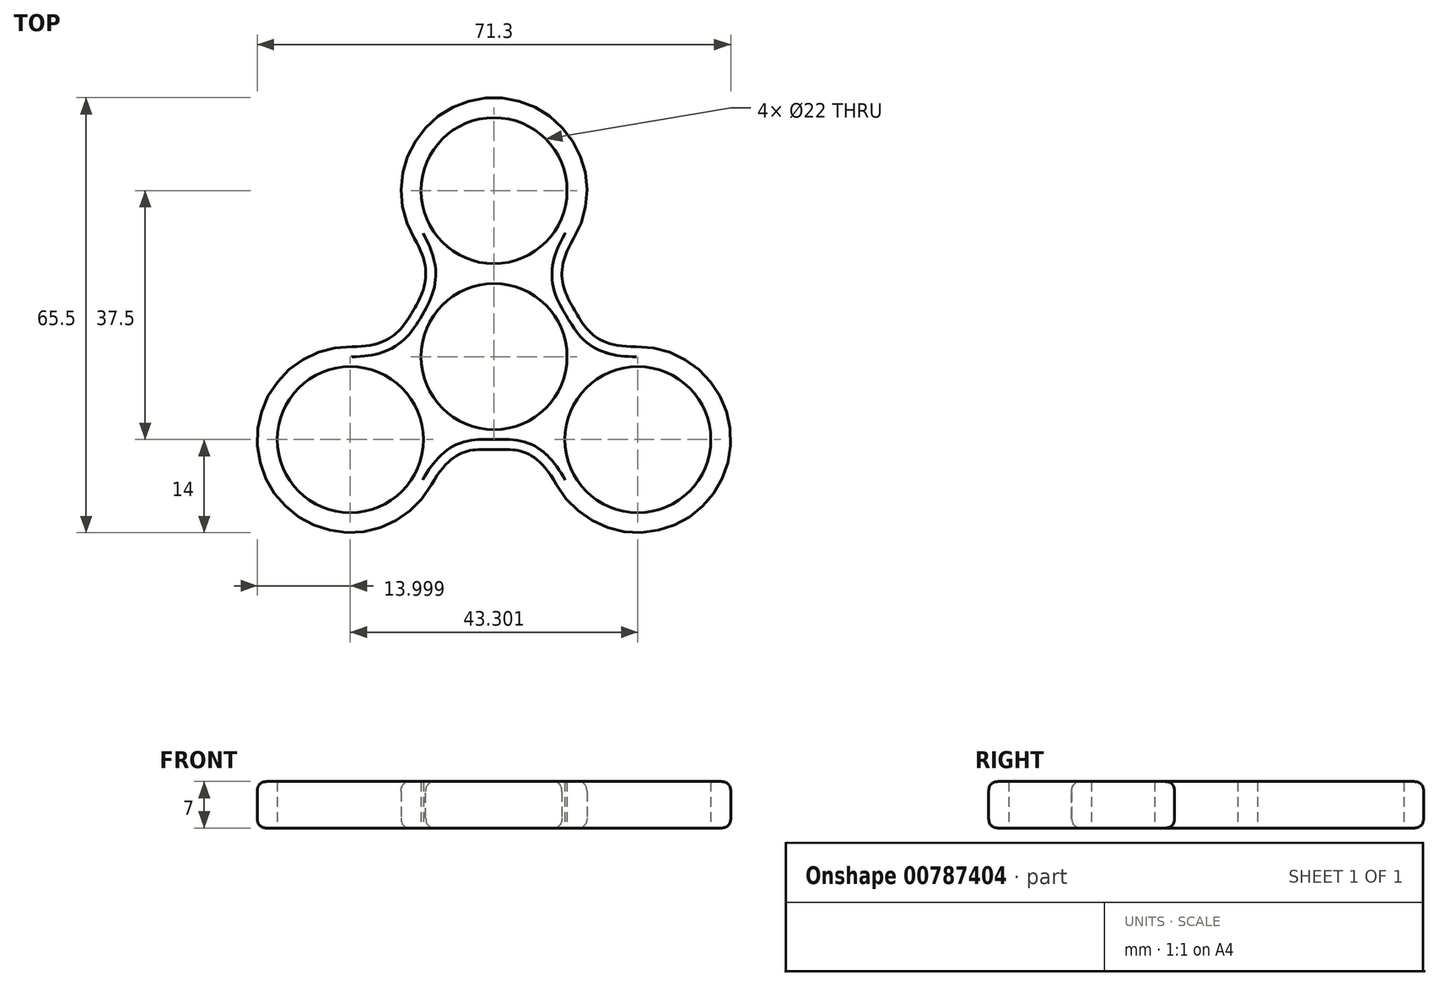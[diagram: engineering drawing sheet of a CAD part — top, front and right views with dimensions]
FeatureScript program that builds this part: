
annotation { "Feature Type Name" : "Feature", "Feature Type Description" : "" }
export const myFeature = defineFeature(function(context is Context, id is Id, definition is map)
    precondition{}
    {
        {
            var Q0;
            Q0=qCreatedBy(makeId("Top.planeOp"),FACE);
            var sketch = newSketch(context, id + "F0", { "sketchPlane" : qUnion([Q0])});
            skCircle(sketch, "E0", {"center": v(0, 0) * mm, "radius": 11 * mm});
            skLineSegment(sketch, "E1", {"start": v(0, 0) * mm, "end": v(0, 25) * mm});
            skLineSegment(sketch, "E2", {"start": v(0, 0) * mm, "end": v(-21.65, -12.5) * mm});
            skLineSegment(sketch, "E3", {"start": v(0, 0) * mm, "end": v(21.65, -12.5) * mm});
            skCircle(sketch, "E4", {"center": v(0, 25) * mm, "radius": 11 * mm});
            skCircle(sketch, "E5", {"center": v(-21.65, -12.5) * mm, "radius": 11 * mm});
            skCircle(sketch, "E6", {"center": v(21.65, -12.5) * mm, "radius": 11 * mm});
            skCircle(sketch, "E7", {"center": v(0, 25) * mm, "radius": 14 * mm});
            skCircle(sketch, "E8", {"center": v(-21.65, -12.5) * mm, "radius": 14 * mm});
            skCircle(sketch, "E9", {"center": v(21.65, -12.5) * mm, "radius": 14 * mm});
            skCircle(sketch, "E10", {"center": v(0, 0) * mm, "radius": 14 * mm});
            skFitSpline(sketch, "E11", {"points": [v(-12, 17.79) * mm, v(-12.12, 7) * mm, v(-21.4, 1.5) * mm], "startDerivative": vector(17.94, -29.85) * mm, "endDerivative": vector(-34.83, 0.6) * mm});
            skFitSpline(sketch, "E12", {"points": [v(12, 17.79) * mm, v(12.12, 7) * mm, v(21.4, 1.5) * mm], "startDerivative": vector(-18.99, -31.6) * mm, "endDerivative": vector(36.86, 0.65) * mm});
            skFitSpline(sketch, "E13", {"points": [v(-9.4, -19.29) * mm, v(0, -14) * mm, v(9.4, -19.29) * mm], "startDerivative": vector(19.58, 35.32) * mm, "endDerivative": vector(19.58, -35.32) * mm});
            skFitSpline(sketch, "E14", {"points": [v(0, 39) * mm, v(24.85, 27.24) * mm, v(24.85, 27.24) * mm, v(24.85, 27.24) * mm, v(12, 17.79) * mm], "startDerivative": vector(95.13, 0) * mm, "endDerivative": vector(-39.1, -74.03) * mm});
            skLineSegment(sketch, "E15.1.0", {"start": v(2.3, -3.98) * mm, "end": v(-19.35, -16.48) * mm});
            skLineSegment(sketch, "E15.2.0", {"start": v(4.6, 0) * mm, "end": v(26.24, -12.5) * mm});
            skPoint(sketch, "E15.center", {"position": v(2.3, -1.33) * mm});
            skPoint(sketch, "E16.1.0", {"position": v(0, 2.65) * mm});
            skPoint(sketch, "E16.2.0", {"position": v(-2.3, -1.33) * mm});
            skLineSegment(sketch, "E17", {"start": v(24.85, 27.24) * mm, "end": v(0, 0) * mm, "construction": true});
            skLineSegment(sketch, "E18.1.0", {"start": v(-36.02, 7.9) * mm, "end": v(0, 0) * mm, "construction": true});
            skLineSegment(sketch, "E18.2.0", {"start": v(11.16, -35.14) * mm, "end": v(0, 0) * mm, "construction": true});
            skFitSpline(sketch, "E19", {"points": [v(33.84, -19.4) * mm, v(11.16, -35.14) * mm, v(11.16, -35.14) * mm, v(9.4, -19.29) * mm], "startDerivative": vector(-47.87, -82.47) * mm, "endDerivative": vector(-25.99, 42.04) * mm});
            skLineSegment(sketch, "E20", {"start": v(11.16, -35.14) * mm, "end": v(11.16, -35.14) * mm});
            skFitSpline(sketch, "E21", {"points": [v(-33.77, -19.5) * mm, v(-36.02, 7.9) * mm, v(-36.02, 7.9) * mm, v(-21.4, 1.5) * mm], "startDerivative": vector(-47.57, 82.39) * mm, "endDerivative": vector(90.33, -4.89) * mm});
            skLineSegment(sketch, "E22", {"start": v(-33.77, -19.5) * mm, "end": v(-42.77, -3.91) * mm, "construction": true});
            skLineSegment(sketch, "E23.1.0", {"start": v(33.77, -19.5) * mm, "end": v(24.77, -35.09) * mm, "construction": true});
            skLineSegment(sketch, "E23.2.0", {"start": v(0, 39) * mm, "end": v(18, 39) * mm, "construction": true});
            skSolve(sketch);
        }
        {
            var Q0;
            {var subQ6=sQuery(id+"F0.wireOp",EDGE,"E4");Q0=makeQuery(id+"F0.imprint","IMPRINT",FACE,{"disambiguationData":[TD([[makeQuery(id+"F0.imprint","IMPRINT",EDGE,{"derivedFrom":subQ6}),-1.0]])]});}
            var Q1;
            {var subQ0=sQuery(id+"F0.wireOp",EDGE,"E10");var subQ3=sQuery(id+"F0.wireOp",EDGE,"E7");var subQ5=makeQuery(id+"F0.imprint","INTERSECT",VERTEX,{"disambiguationData":[OD(1.0)],"derivedFrom":[subQ3,subQ0]});Q1=makeQuery(id+"F0.imprint","IMPRINT",FACE,{"disambiguationData":[TD([[makeQuery(id+"F0.imprint","IMPRINT",EDGE,{"disambiguationData":[TD([[subQ5,1.0]])],"derivedFrom":subQ3}),1.0]])]});}
            var Q2;
            {var subQ0=sQuery(id+"F0.wireOp",EDGE,"E10");var subQ3=sQuery(id+"F0.wireOp",EDGE,"E7");var subQ5=makeQuery(id+"F0.imprint","INTERSECT",VERTEX,{"disambiguationData":[OD(0.0)],"derivedFrom":[subQ3,subQ0]});Q2=makeQuery(id+"F0.imprint","IMPRINT",FACE,{"disambiguationData":[TD([[makeQuery(id+"F0.imprint","IMPRINT",EDGE,{"disambiguationData":[TD([[subQ5,-1.0]])],"derivedFrom":subQ3}),1.0]])]});}
            var Q3;
            {var subQ0=sQuery(id+"F0.wireOp",EDGE,"E12");var subQ1=sQuery(id+"F0.wireOp",EDGE,"E7");var subQ2=makeQuery(id+"F0.imprint","INTERSECT",VERTEX,{"derivedFrom":[subQ1,subQ0]});Q3=makeQuery(id+"F0.imprint","IMPRINT",FACE,{"disambiguationData":[TD([[makeQuery(id+"F0.imprint","IMPRINT",EDGE,{"disambiguationData":[TD([[subQ2,1.0]])],"derivedFrom":subQ1}),-1.0]])]});}
            var Q4;
            {var subQ0=sQuery(id+"F0.wireOp",EDGE,"E10");var subQ8=makeQuery(id+"F0.imprint","INTERSECT",VERTEX,{"derivedFrom":[subQ0,sQuery(id+"F0.wireOp",EDGE,"E12")]});Q4=makeQuery(id+"F0.imprint","IMPRINT",FACE,{"disambiguationData":[TD([[makeQuery(id+"F0.imprint","IMPRINT",EDGE,{"disambiguationData":[TD([[subQ8,-1.0]])],"derivedFrom":subQ0}),1.0]])]});}
            var Q5;
            {var subQ0=sQuery(id+"F0.wireOp",EDGE,"E11");var subQ1=sQuery(id+"F0.wireOp",EDGE,"E7");var subQ2=makeQuery(id+"F0.imprint","INTERSECT",VERTEX,{"derivedFrom":[subQ1,subQ0]});Q5=makeQuery(id+"F0.imprint","IMPRINT",FACE,{"disambiguationData":[TD([[makeQuery(id+"F0.imprint","IMPRINT",EDGE,{"disambiguationData":[TD([[subQ2,-1.0]])],"derivedFrom":subQ1}),-1.0]])]});}
            var Q6;
            {var subQ0=sQuery(id+"F0.wireOp",EDGE,"E10");var subQ8=makeQuery(id+"F0.imprint","INTERSECT",VERTEX,{"derivedFrom":[subQ0,sQuery(id+"F0.wireOp",EDGE,"E11")]});Q6=makeQuery(id+"F0.imprint","IMPRINT",FACE,{"disambiguationData":[TD([[makeQuery(id+"F0.imprint","IMPRINT",EDGE,{"disambiguationData":[TD([[subQ8,1.0]])],"derivedFrom":subQ0}),1.0]])]});}
            var Q7;
            {var subQ0=sQuery(id+"F0.wireOp",EDGE,"E11");var subQ1=sQuery(id+"F0.wireOp",EDGE,"E8");var subQ2=makeQuery(id+"F0.imprint","INTERSECT",VERTEX,{"derivedFrom":[subQ1,subQ0]});Q7=makeQuery(id+"F0.imprint","IMPRINT",FACE,{"disambiguationData":[TD([[makeQuery(id+"F0.imprint","IMPRINT",EDGE,{"disambiguationData":[TD([[subQ2,1.0]])],"derivedFrom":subQ1}),-1.0]])]});}
            var Q8;
            {var subQ0=sQuery(id+"F0.wireOp",EDGE,"E10");var subQ3=sQuery(id+"F0.wireOp",EDGE,"E8");var subQ5=makeQuery(id+"F0.imprint","INTERSECT",VERTEX,{"disambiguationData":[OD(1.0)],"derivedFrom":[subQ3,subQ0]});Q8=makeQuery(id+"F0.imprint","IMPRINT",FACE,{"disambiguationData":[TD([[makeQuery(id+"F0.imprint","IMPRINT",EDGE,{"disambiguationData":[TD([[subQ5,1.0]])],"derivedFrom":subQ3}),1.0]])]});}
            var Q9;
            {var subQ0=sQuery(id+"F0.wireOp",EDGE,"E10");var subQ3=sQuery(id+"F0.wireOp",EDGE,"E8");var subQ5=makeQuery(id+"F0.imprint","INTERSECT",VERTEX,{"disambiguationData":[OD(0.0)],"derivedFrom":[subQ3,subQ0]});Q9=makeQuery(id+"F0.imprint","IMPRINT",FACE,{"disambiguationData":[TD([[makeQuery(id+"F0.imprint","IMPRINT",EDGE,{"disambiguationData":[TD([[subQ5,-1.0]])],"derivedFrom":subQ3}),1.0]])]});}
            var Q10;
            {var subQ4=sQuery(id+"F0.wireOp",EDGE,"E5");Q10=makeQuery(id+"F0.imprint","IMPRINT",FACE,{"disambiguationData":[TD([[makeQuery(id+"F0.imprint","IMPRINT",EDGE,{"derivedFrom":subQ4}),-1.0]])]});}
            var Q11;
            {var subQ0=sQuery(id+"F0.wireOp",EDGE,"E13");var subQ1=sQuery(id+"F0.wireOp",EDGE,"E8");var subQ2=makeQuery(id+"F0.imprint","INTERSECT",VERTEX,{"derivedFrom":[subQ1,subQ0]});Q11=makeQuery(id+"F0.imprint","IMPRINT",FACE,{"disambiguationData":[TD([[makeQuery(id+"F0.imprint","IMPRINT",EDGE,{"disambiguationData":[TD([[subQ2,-1.0]])],"derivedFrom":subQ1}),-1.0]])]});}
            var Q12;
            {var subQ0=sQuery(id+"F0.wireOp",EDGE,"E13");var subQ1=sQuery(id+"F0.wireOp",EDGE,"E9");var subQ2=makeQuery(id+"F0.imprint","INTERSECT",VERTEX,{"derivedFrom":[subQ1,subQ0]});Q12=makeQuery(id+"F0.imprint","IMPRINT",FACE,{"disambiguationData":[TD([[makeQuery(id+"F0.imprint","IMPRINT",EDGE,{"disambiguationData":[TD([[subQ2,1.0]])],"derivedFrom":subQ1}),-1.0]])]});}
            var Q13;
            {var subQ0=sQuery(id+"F0.wireOp",EDGE,"E10");var subQ3=sQuery(id+"F0.wireOp",EDGE,"E9");var subQ5=makeQuery(id+"F0.imprint","INTERSECT",VERTEX,{"disambiguationData":[OD(1.0)],"derivedFrom":[subQ3,subQ0]});Q13=makeQuery(id+"F0.imprint","IMPRINT",FACE,{"disambiguationData":[TD([[makeQuery(id+"F0.imprint","IMPRINT",EDGE,{"disambiguationData":[TD([[subQ5,1.0]])],"derivedFrom":subQ3}),1.0]])]});}
            var Q14;
            {var subQ0=sQuery(id+"F0.wireOp",EDGE,"E10");var subQ3=sQuery(id+"F0.wireOp",EDGE,"E9");var subQ5=makeQuery(id+"F0.imprint","INTERSECT",VERTEX,{"disambiguationData":[OD(0.0)],"derivedFrom":[subQ3,subQ0]});Q14=makeQuery(id+"F0.imprint","IMPRINT",FACE,{"disambiguationData":[TD([[makeQuery(id+"F0.imprint","IMPRINT",EDGE,{"disambiguationData":[TD([[subQ5,-1.0]])],"derivedFrom":subQ3}),1.0]])]});}
            var Q15;
            {var subQ0=sQuery(id+"F0.wireOp",EDGE,"E10");var subQ1=makeQuery(id+"F0.imprint","INTERSECT",VERTEX,{"derivedFrom":[subQ0,sQuery(id+"F0.wireOp",EDGE,"E13")]});Q15=makeQuery(id+"F0.imprint","IMPRINT",FACE,{"disambiguationData":[TD([[makeQuery(id+"F0.imprint","IMPRINT",EDGE,{"disambiguationData":[TD([[subQ1,1.0]])],"derivedFrom":subQ0}),1.0]])]});}
            var Q16;
            {var subQ0=sQuery(id+"F0.wireOp",EDGE,"E12");var subQ1=sQuery(id+"F0.wireOp",EDGE,"E9");var subQ2=makeQuery(id+"F0.imprint","INTERSECT",VERTEX,{"derivedFrom":[subQ1,subQ0]});Q16=makeQuery(id+"F0.imprint","IMPRINT",FACE,{"disambiguationData":[TD([[makeQuery(id+"F0.imprint","IMPRINT",EDGE,{"disambiguationData":[TD([[subQ2,-1.0]])],"derivedFrom":subQ1}),-1.0]])]});}
            var Q17;
            {var subQ0=sQuery(id+"F0.wireOp",EDGE,"E15.1.0");var subQ1=sQuery(id+"F0.wireOp",EDGE,"E0");var subQ2=makeQuery(id+"F0.imprint","INTERSECT",VERTEX,{"derivedFrom":[subQ1,subQ0]});Q17=makeQuery(id+"F0.imprint","IMPRINT",FACE,{"disambiguationData":[TD([[makeQuery(id+"F0.imprint","IMPRINT",EDGE,{"disambiguationData":[TD([[subQ2,-1.0]])],"derivedFrom":subQ0}),-1.0]])]});}
            var Q18;
            {var subQ3=sQuery(id+"F0.wireOp",EDGE,"E8");var subQ5=sQuery(id+"F0.wireOp",EDGE,"E15.1.0");var subQ6=makeQuery(id+"F0.imprint","INTERSECT",VERTEX,{"derivedFrom":[subQ3,subQ5]});Q18=makeQuery(id+"F0.imprint","IMPRINT",FACE,{"disambiguationData":[TD([[makeQuery(id+"F0.imprint","IMPRINT",EDGE,{"disambiguationData":[TD([[subQ6,-1.0]])],"derivedFrom":subQ5}),-1.0]])]});}
            var Q19;
            {var subQ0=sQuery(id+"F0.wireOp",EDGE,"E21");Q19=makeQuery(id+"F0.imprint","IMPRINT",FACE,{"disambiguationData":[TD([[makeQuery(id+"F0.imprint","IMPRINT",EDGE,{"derivedFrom":subQ0}),-1.0]])]});}
            var Q20;
            {var subQ1=sQuery(id+"F0.wireOp",EDGE,"E8");var subQ6=makeQuery(id+"F0.imprint","INTERSECT",VERTEX,{"derivedFrom":[subQ1,sQuery(id+"F0.wireOp",EDGE,"E13")]});Q20=makeQuery(id+"F0.imprint","IMPRINT",FACE,{"disambiguationData":[TD([[makeQuery(id+"F0.imprint","IMPRINT",EDGE,{"disambiguationData":[TD([[subQ6,1.0]])],"derivedFrom":subQ1}),1.0]])]});}
            var Q21;
            {var subQ0=sQuery(id+"F0.wireOp",EDGE,"E19");var subQ1=sQuery(id+"F0.wireOp",EDGE,"E9");var subQ2=makeQuery(id+"F0.imprint","INTERSECT",VERTEX,{"disambiguationData":[OD(1.0)],"derivedFrom":[subQ1,subQ0]});Q21=makeQuery(id+"F0.imprint","IMPRINT",FACE,{"disambiguationData":[TD([[makeQuery(id+"F0.imprint","IMPRINT",EDGE,{"disambiguationData":[TD([[subQ2,-1.0]])],"derivedFrom":subQ1}),-1.0]])]});}
            var Q22;
            {var subQ3=sQuery(id+"F0.wireOp",EDGE,"E9");var subQ5=sQuery(id+"F0.wireOp",EDGE,"E15.2.0");var subQ7=makeQuery(id+"F0.imprint","INTERSECT",VERTEX,{"derivedFrom":[subQ3,subQ5]});Q22=makeQuery(id+"F0.imprint","IMPRINT",FACE,{"disambiguationData":[TD([[makeQuery(id+"F0.imprint","IMPRINT",EDGE,{"disambiguationData":[TD([[subQ7,-1.0]])],"derivedFrom":subQ5}),-1.0]])]});}
            var Q23;
            {var subQ0=sQuery(id+"F0.wireOp",EDGE,"E15.2.0");var subQ1=sQuery(id+"F0.wireOp",EDGE,"E0");var subQ2=makeQuery(id+"F0.imprint","INTERSECT",VERTEX,{"derivedFrom":[subQ1,subQ0]});Q23=makeQuery(id+"F0.imprint","IMPRINT",FACE,{"disambiguationData":[TD([[makeQuery(id+"F0.imprint","IMPRINT",EDGE,{"disambiguationData":[TD([[subQ2,-1.0]])],"derivedFrom":subQ0}),-1.0]])]});}
            var Q24;
            {var subQ1=sQuery(id+"F0.wireOp",EDGE,"E9");var subQ8=makeQuery(id+"F0.imprint","INTERSECT",VERTEX,{"derivedFrom":[subQ1,sQuery(id+"F0.wireOp",EDGE,"E12")]});Q24=makeQuery(id+"F0.imprint","IMPRINT",FACE,{"disambiguationData":[TD([[makeQuery(id+"F0.imprint","IMPRINT",EDGE,{"disambiguationData":[TD([[subQ8,-1.0]])],"derivedFrom":subQ1}),1.0]])]});}
            var Q25;
            {var subQ0=sQuery(id+"F0.wireOp",EDGE,"E15.2.0");var subQ1=sQuery(id+"F0.wireOp",EDGE,"E6");var subQ2=makeQuery(id+"F0.imprint","INTERSECT",VERTEX,{"derivedFrom":[subQ1,subQ0]});Q25=makeQuery(id+"F0.imprint","IMPRINT",FACE,{"disambiguationData":[TD([[makeQuery(id+"F0.imprint","IMPRINT",EDGE,{"disambiguationData":[TD([[subQ2,1.0]])],"derivedFrom":subQ0}),-1.0]])]});}
            var Q26;
            {var subQ0=sQuery(id+"F0.wireOp",EDGE,"E14");var subQ1=sQuery(id+"F0.wireOp",EDGE,"E7");var subQ2=makeQuery(id+"F0.imprint","INTERSECT",VERTEX,{"disambiguationData":[OD(0.0)],"derivedFrom":[subQ1,subQ0]});Q26=makeQuery(id+"F0.imprint","IMPRINT",FACE,{"disambiguationData":[TD([[makeQuery(id+"F0.imprint","IMPRINT",EDGE,{"disambiguationData":[TD([[subQ2,1.0]])],"derivedFrom":subQ1}),-1.0]])]});}
            extrude(context, id + "F1", {"entities" : qUnion([Q0, Q1, Q2, Q3, Q4, Q5, Q6, Q7, Q8, Q9, Q10, Q11, Q12, Q13, Q14, Q15, Q16, Q17, Q18, Q19, Q20, Q21, Q22, Q23, Q24, Q25, Q26]), "depth" : 7 * mm, "offsetDistance" : 25 * mm});
        }
        {
            var Q0;
            Q0=makeQuery(id+"F1.opExtrude","CAP_EDGE",EDGE,{"disambiguationData":[OSD([sQuery(id+"F0.wireOp",EDGE,"E11")])],"isStart":false});
            var Q1;
            Q1=makeQuery(id+"F1.opExtrude","CAP_EDGE",EDGE,{"disambiguationData":[OSD([sQuery(id+"F0.wireOp",EDGE,"E8")])],"isStart":false});
            var Q2;
            Q2=makeQuery(id+"F1.opExtrude","CAP_EDGE",EDGE,{"disambiguationData":[OSD([sQuery(id+"F0.wireOp",EDGE,"E13")])],"isStart":false});
            var Q3;
            Q3=makeQuery(id+"F1.opExtrude","CAP_EDGE",EDGE,{"disambiguationData":[OSD([sQuery(id+"F0.wireOp",EDGE,"E9")])],"isStart":false});
            var Q4;
            Q4=makeQuery(id+"F1.opExtrude","CAP_EDGE",EDGE,{"disambiguationData":[OSD([sQuery(id+"F0.wireOp",EDGE,"E12")])],"isStart":false});
            var Q5;
            Q5=makeQuery(id+"F1.opExtrude","CAP_EDGE",EDGE,{"disambiguationData":[OSD([sQuery(id+"F0.wireOp",EDGE,"E7")])],"isStart":false});
            var Q6;
            Q6=makeQuery(id+"F1.opExtrude","CAP_EDGE",EDGE,{"disambiguationData":[OSD([sQuery(id+"F0.wireOp",EDGE,"E14")])],"isStart":false});
            var Q7;
            Q7=makeQuery(id+"F1.opExtrude","CAP_EDGE",EDGE,{"disambiguationData":[OSD([sQuery(id+"F0.wireOp",EDGE,"E7")])],"isStart":true});
            var Q8;
            Q8=makeQuery(id+"F1.opExtrude","CAP_EDGE",EDGE,{"disambiguationData":[OSD([sQuery(id+"F0.wireOp",EDGE,"E12")])],"isStart":true});
            var Q9;
            Q9=makeQuery(id+"F1.opExtrude","CAP_EDGE",EDGE,{"disambiguationData":[OSD([sQuery(id+"F0.wireOp",EDGE,"E14")])],"isStart":true});
            var Q10;
            Q10=makeQuery(id+"F1.opExtrude","CAP_EDGE",EDGE,{"disambiguationData":[OSD([sQuery(id+"F0.wireOp",EDGE,"E11")])],"isStart":true});
            var Q11;
            Q11=makeQuery(id+"F1.opExtrude","CAP_EDGE",EDGE,{"disambiguationData":[OSD([sQuery(id+"F0.wireOp",EDGE,"E8")])],"isStart":true});
            var Q12;
            Q12=makeQuery(id+"F1.opExtrude","CAP_EDGE",EDGE,{"disambiguationData":[OSD([sQuery(id+"F0.wireOp",EDGE,"E13")])],"isStart":true});
            var Q13;
            Q13=makeQuery(id+"F1.opExtrude","CAP_EDGE",EDGE,{"disambiguationData":[OSD([sQuery(id+"F0.wireOp",EDGE,"E9")])],"isStart":true});
            var Q14;
            Q14=makeQuery(id+"F1.opExtrude","CAP_EDGE",EDGE,{"disambiguationData":[OSD([sQuery(id+"F0.wireOp",EDGE,"E19")])],"isStart":false});
            var Q15;
            Q15=makeQuery(id+"F1.opExtrude","CAP_EDGE",EDGE,{"disambiguationData":[OSD([sQuery(id+"F0.wireOp",EDGE,"E21")])],"isStart":false});
            var Q16;
            Q16=makeQuery(id+"F1.opExtrude","CAP_EDGE",EDGE,{"disambiguationData":[OSD([sQuery(id+"F0.wireOp",EDGE,"E21")])],"isStart":true});
            var Q17;
            Q17=makeQuery(id+"F1.opExtrude","CAP_EDGE",EDGE,{"disambiguationData":[OSD([sQuery(id+"F0.wireOp",EDGE,"E19")])],"isStart":true});
            fillet(context, id + "F2", {"entities" : qUnion([Q0, Q1, Q2, Q3, Q4, Q5, Q6, Q7, Q8, Q9, Q10, Q11, Q12, Q13, Q14, Q15, Q16, Q17]), "radius" : 1.5 * mm, "rho" : 0.5, "crossSection" : FilletCrossSection.CONIC, "allowEdgeOverflow" : false});
        }
    });
